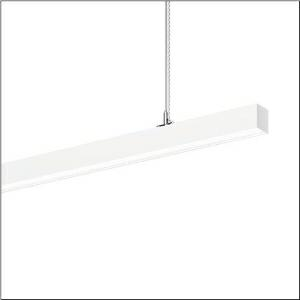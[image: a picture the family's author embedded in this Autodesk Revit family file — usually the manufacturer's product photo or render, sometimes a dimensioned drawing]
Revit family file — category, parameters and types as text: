
# Revit family: silica_r__21_51mx33tctdw_01d4
name_source: partatom
category: Lighting Fixtures
units: mm (PartAtom-declared; Revit-internal decimal feet)

## family parameters
Cut with Voids When Loaded = No
Host = Face
Light Source = No
Part Type = Normal
Room Calculation Point = No
Round Connector Dimension = Use Diameter
Shared = No

## types (1)
- --- (1 x LED, 14340 lm, 134.7 W, 6500K)
    Apparent Load = 135 VA
    CIE Flux Codes = 78 96 99 56 100
    Color Rendering = 80
    Color Temperature = 6500K
    Default Elevation = 1800 mm
    Description = Silica® 21, office luminaire, primary optical cover: prismatic diffuser, of PMMA, CAT 2 (L<= 3000cd/m²), light emission: direct/indirect distribution, primary light characteristic: symmetric, installation type: suspended mounting, LED, rated luminous flux: 14.340lm, luminous efficacy: 101lm/W, light colour: 8tw, colour temperature: 2700..6500K, control gear: DALI DT8, with terminal, 3+2-pole, max. 2.5mm², mains connection: 220..240V, AC, 50/60Hz, rated input power: 141.4W, luminaire housing, of aluminium, traffic white (RAL 9016), length: 3.004mm, width: 53mm, height: 53mm, protection rating (complete): IP20, insulation class (complete): insulation class I (protective earthing), certification: CE, permissible operating ambient temperature: 0..+35°C, standard: EN 50419, packaging unit: 1 piece
    Height = 53 mm
    Lamp = 1 x LED
    Lamp Light Flux = 14340 lm
    Lamp Power = 134.7 W
    Lamp count = 1
    Length = 3004 mm
    Luminous efficacy = 106 lm/W
    Manufacturer = Siteco
    ModVariant = No
    Model = 51MX33TCTDW
    Mounting Place = Ceiling
    Mounting Type = Pendant
    Number of Poles = 1
    OnlyDefault = Yes
    Power Factor = 1
    Product Name = Silica® 21
    Product group = office luminaire | ceiling pendant
    ProductGroupID = 904
    Protection Class = Protection class I
    Protection Degree = IP 20
    RLX_Detail_Level = 1
    RLX_Emergency_Light_Flux = 0 lm
    RLX_Emergency_Type = 0
    RLX_Emergency_Type_DB = No
    RlxData = <blob elided: 18093 chars, md5=bd10dca6>
    Socket = socket
    Standby Power = 0 W
    System Light Flux = 14340 lm
    System Power = 135 W
    Type Comments = individual setting
    Type Image = l_1349007.jpg
    URL = http://relux.com
    VarID = @adj_139770
    Voltage = 0 V
    Weight = 0.00 kg
    Width = 53 mm

## geometry (parser evidence)
native form markers: Blend x4, Sweep x13
no freeform markers — native parametric forms only
